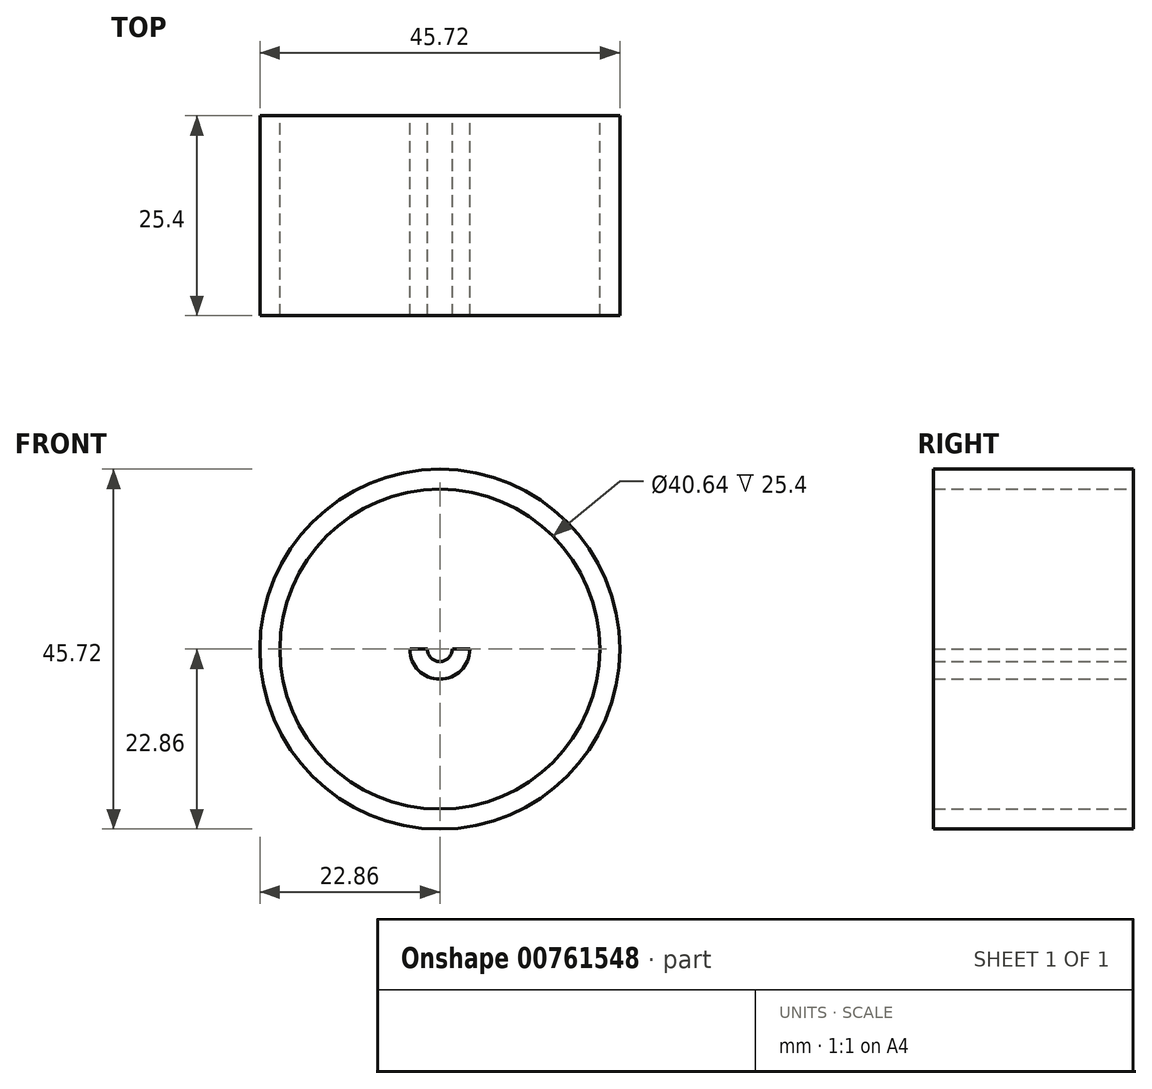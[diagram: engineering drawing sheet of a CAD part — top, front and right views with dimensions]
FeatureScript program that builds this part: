
annotation { "Feature Type Name" : "Feature", "Feature Type Description" : "" }
export const myFeature = defineFeature(function(context is Context, id is Id, definition is map)
    precondition{}
    {
        {
            var Q0;
            Q0=qCreatedBy(makeId("Front.planeOp"),FACE);
            var sketch = newSketch(context, id + "F0", { "sketchPlane" : qUnion([Q0])});
            skCircle(sketch, "E0", {"center": v(0, 0) * mm, "radius": 22.86 * mm});
            skCircle(sketch, "E1", {"center": v(0, 0) * mm, "radius": 1.59 * mm});
            skCircle(sketch, "E2", {"center": v(0, 0) * mm, "radius": 3.81 * mm});
            skCircle(sketch, "E3.0", {"center": v(0, 0) * mm, "radius": 20.32 * mm});
            skLineSegment(sketch, "E4", {"start": v(0, 0) * mm, "end": v(0, 3.81) * mm});
            skLineSegment(sketch, "E5", {"start": v(0, 3.81) * mm, "end": v(0, -3.81) * mm});
            skLineSegment(sketch, "E6", {"start": v(0, -3.81) * mm, "end": v(0, 0) * mm});
            skLineSegment(sketch, "E7", {"start": v(3.81, 0) * mm, "end": v(-3.81, 0) * mm});
            skLineSegment(sketch, "E8", {"start": v(0, 3.8) * mm, "end": v(0, 11.02) * mm});
            skLineSegment(sketch, "E9", {"start": v(-1.49, 15.1) * mm, "end": v(-5.28, 19.62) * mm});
            skPoint(sketch, "E10.newPointA", {"position": v(0, 13.33) * mm});
            skArc(sketch, "E10.filletArc", {"start": v(0, 11.02) * mm, "mid": v(-0.38, 13.2) * mm, "end": v(-1.49, 15.1) * mm});
            skLineSegment(sketch, "E11", {"start": v(0.96, 3.69) * mm, "end": v(3.31, 12.87) * mm});
            skLineSegment(sketch, "E12", {"start": v(2.89, 17.19) * mm, "end": v(1.41, 20.27) * mm});
            skPoint(sketch, "E13.end.orphan", {"position": v(7.48, 13.33) * mm});
            skPoint(sketch, "E14.newPointA", {"position": v(3.89, 15.1) * mm});
            skArc(sketch, "E14.filletArc", {"start": v(3.31, 12.87) * mm, "mid": v(3.48, 15.06) * mm, "end": v(2.89, 17.19) * mm});
            skLineSegment(sketch, "E15", {"start": v(0.55, 7.3) * mm, "end": v(1, 13.07) * mm});
            skLineSegment(sketch, "E16", {"start": v(2.28, 13.03) * mm, "end": v(1.06, 7.23) * mm});
            skLineSegment(sketch, "E17", {"start": v(0.81, 7.03) * mm, "end": v(0.8, 7.03) * mm});
            skLineSegment(sketch, "E18", {"start": v(2.26, 13.24) * mm, "end": v(0.27, 18.44) * mm});
            skLineSegment(sketch, "E19", {"start": v(0.95, 13.3) * mm, "end": v(-1.71, 17.52) * mm});
            skLineSegment(sketch, "E20", {"start": v(-0.71, 18.88) * mm, "end": v(-1.34, 18.64) * mm});
            skPoint(sketch, "E21.start.orphan", {"position": v(-2.74, 19.15) * mm});
            skPoint(sketch, "E22.visualSharp", {"position": v(-2.2, 18.3) * mm});
            skArc(sketch, "E22.filletArc", {"start": v(-1.34, 18.64) * mm, "mid": v(-1.8, 18.17) * mm, "end": v(-1.71, 17.52) * mm});
            skPoint(sketch, "E23.visualSharp", {"position": v(0, 19.15) * mm});
            skArc(sketch, "E23.filletArc", {"start": v(0.27, 18.44) * mm, "mid": v(-0.13, 18.86) * mm, "end": v(-0.71, 18.88) * mm});
            skPoint(sketch, "E24.visualSharp", {"position": v(2.3, 13.14) * mm});
            skArc(sketch, "E24.filletArc", {"start": v(2.28, 13.03) * mm, "mid": v(2.29, 13.13) * mm, "end": v(2.26, 13.24) * mm});
            skPoint(sketch, "E25.visualSharp", {"position": v(1.02, 13.2) * mm});
            skArc(sketch, "E25.filletArc", {"start": v(1, 13.07) * mm, "mid": v(1, 13.2) * mm, "end": v(0.95, 13.3) * mm});
            skPoint(sketch, "E26.visualSharp", {"position": v(0.53, 7.03) * mm});
            skArc(sketch, "E26.filletArc", {"start": v(0.55, 7.3) * mm, "mid": v(0.62, 7.1) * mm, "end": v(0.8, 7.03) * mm});
            skPoint(sketch, "E27.visualSharp", {"position": v(1.02, 7.03) * mm});
            skArc(sketch, "E27.filletArc", {"start": v(0.81, 7.03) * mm, "mid": v(0.97, 7.08) * mm, "end": v(1.06, 7.23) * mm});
            skArc(sketch, "E28.1.0", {"start": v(-11.64, 14.3) * mm, "mid": v(-12.22, 14.37) * mm, "end": v(-12.68, 14) * mm});
            skLineSegment(sketch, "E28.1.1", {"start": v(-12.68, 14) * mm, "end": v(-13, 13.42) * mm});
            skArc(sketch, "E28.1.2", {"start": v(-13, 13.42) * mm, "mid": v(-13.05, 12.77) * mm, "end": v(-12.57, 12.32) * mm});
            skLineSegment(sketch, "E28.1.3", {"start": v(-7.83, 10.8) * mm, "end": v(-12.57, 12.32) * mm});
            skLineSegment(sketch, "E28.1.4", {"start": v(-6.78, 11.6) * mm, "end": v(-11.64, 14.3) * mm});
            skLineSegment(sketch, "E28.1.5", {"start": v(-6.63, 11.44) * mm, "end": v(-3.83, 6.22) * mm});
            skLineSegment(sketch, "E28.1.6", {"start": v(-4.27, 5.95) * mm, "end": v(-7.63, 10.66) * mm});
            skLineSegment(sketch, "E28.1.7", {"start": v(-1.63, 3.44) * mm, "end": v(-5.73, 11.99) * mm});
            skLineSegment(sketch, "E28.1.8", {"start": v(-2.45, 2.92) * mm, "end": v(-7.09, 8.44) * mm});
            skLineSegment(sketch, "E28.1.9", {"start": v(-10.85, 10.62) * mm, "end": v(-16.66, 11.64) * mm});
            skLineSegment(sketch, "E28.1.10", {"start": v(-8.84, 15.02) * mm, "end": v(-11.95, 16.44) * mm});
            skArc(sketch, "E28.1.11", {"start": v(-5.73, 11.99) * mm, "mid": v(-7.02, 13.78) * mm, "end": v(-8.84, 15.02) * mm});
            skArc(sketch, "E28.1.12", {"start": v(-7.09, 8.44) * mm, "mid": v(-8.77, 9.86) * mm, "end": v(-10.85, 10.62) * mm});
            skArc(sketch, "E28.1.13", {"start": v(-6.63, 11.44) * mm, "mid": v(-6.7, 11.53) * mm, "end": v(-6.78, 11.6) * mm});
            skArc(sketch, "E28.1.14", {"start": v(-7.63, 10.66) * mm, "mid": v(-7.72, 10.75) * mm, "end": v(-7.83, 10.8) * mm});
            skArc(sketch, "E28.1.15", {"start": v(-4.27, 5.95) * mm, "mid": v(-4.1, 5.84) * mm, "end": v(-3.9, 5.9) * mm});
            skArc(sketch, "E28.1.16", {"start": v(-3.9, 5.9) * mm, "mid": v(-3.8, 6.05) * mm, "end": v(-3.83, 6.22) * mm});
            skArc(sketch, "E28.2.0", {"start": v(-18.11, 3.47) * mm, "mid": v(-18.6, 3.15) * mm, "end": v(-18.72, 2.58) * mm});
            skLineSegment(sketch, "E28.2.1", {"start": v(-18.72, 2.58) * mm, "end": v(-18.59, 1.92) * mm});
            skArc(sketch, "E28.2.2", {"start": v(-18.59, 1.92) * mm, "mid": v(-18.2, 1.4) * mm, "end": v(-17.55, 1.36) * mm});
            skLineSegment(sketch, "E28.2.3", {"start": v(-12.94, 3.25) * mm, "end": v(-17.55, 1.36) * mm});
            skLineSegment(sketch, "E28.2.4", {"start": v(-12.65, 4.53) * mm, "end": v(-18.11, 3.47) * mm});
            skLineSegment(sketch, "E28.2.5", {"start": v(-12.43, 4.5) * mm, "end": v(-6.93, 2.3) * mm});
            skLineSegment(sketch, "E28.2.6", {"start": v(-7.1, 1.8) * mm, "end": v(-12.7, 3.26) * mm});
            skLineSegment(sketch, "E28.2.7", {"start": v(-3.46, 1.59) * mm, "end": v(-12.1, 5.5) * mm});
            skLineSegment(sketch, "E28.2.8", {"start": v(-3.75, 0.66) * mm, "end": v(-10.86, 1.91) * mm});
            skLineSegment(sketch, "E28.2.9", {"start": v(-15.13, 1.16) * mm, "end": v(-20.24, -1.79) * mm});
            skLineSegment(sketch, "E28.2.10", {"start": v(-16.43, 5.83) * mm, "end": v(-19.72, 4.9) * mm});
            skArc(sketch, "E28.2.11", {"start": v(-12.1, 5.5) * mm, "mid": v(-14.23, 6.05) * mm, "end": v(-16.43, 5.83) * mm});
            skArc(sketch, "E28.2.12", {"start": v(-10.86, 1.91) * mm, "mid": v(-13.06, 1.91) * mm, "end": v(-15.13, 1.16) * mm});
            skArc(sketch, "E28.2.13", {"start": v(-12.43, 4.5) * mm, "mid": v(-12.54, 4.53) * mm, "end": v(-12.65, 4.53) * mm});
            skArc(sketch, "E28.2.14", {"start": v(-12.7, 3.26) * mm, "mid": v(-12.82, 3.27) * mm, "end": v(-12.94, 3.25) * mm});
            skArc(sketch, "E28.2.15", {"start": v(-7.1, 1.8) * mm, "mid": v(-6.9, 1.84) * mm, "end": v(-6.78, 2.01) * mm});
            skArc(sketch, "E28.2.16", {"start": v(-6.78, 2.02) * mm, "mid": v(-6.8, 2.19) * mm, "end": v(-6.93, 2.3) * mm});
            skArc(sketch, "E28.3.0", {"start": v(-16.1, -8.98) * mm, "mid": v(-16.27, -9.54) * mm, "end": v(-16, -10.06) * mm});
            skLineSegment(sketch, "E28.3.1", {"start": v(-16, -10.06) * mm, "end": v(-15.47, -10.48) * mm});
            skArc(sketch, "E28.3.2", {"start": v(-15.47, -10.48) * mm, "mid": v(-14.84, -10.63) * mm, "end": v(-14.32, -10.24) * mm});
            skLineSegment(sketch, "E28.3.3", {"start": v(-12, -5.83) * mm, "end": v(-14.32, -10.24) * mm});
            skLineSegment(sketch, "E28.3.4", {"start": v(-12.6, -4.66) * mm, "end": v(-16.1, -8.98) * mm});
            skLineSegment(sketch, "E28.3.5", {"start": v(-12.42, -4.54) * mm, "end": v(-6.79, -2.7) * mm});
            skLineSegment(sketch, "E28.3.6", {"start": v(-6.6, -3.17) * mm, "end": v(-11.83, -5.66) * mm});
            skLineSegment(sketch, "E28.3.7", {"start": v(-3.67, -1.01) * mm, "end": v(-12.8, -3.56) * mm});
            skLineSegment(sketch, "E28.3.8", {"start": v(-3.3, -1.9) * mm, "end": v(-9.55, -5.51) * mm});
            skLineSegment(sketch, "E28.3.9", {"start": v(-12.34, -8.84) * mm, "end": v(-14.36, -14.38) * mm});
            skLineSegment(sketch, "E28.3.10", {"start": v(-16.33, -6.1) * mm, "end": v(-18.26, -8.91) * mm});
            skArc(sketch, "E28.3.11", {"start": v(-12.8, -3.56) * mm, "mid": v(-14.79, -4.52) * mm, "end": v(-16.33, -6.1) * mm});
            skArc(sketch, "E28.3.12", {"start": v(-9.55, -5.51) * mm, "mid": v(-11.24, -6.93) * mm, "end": v(-12.34, -8.84) * mm});
            skArc(sketch, "E28.3.13", {"start": v(-12.42, -4.54) * mm, "mid": v(-12.52, -4.59) * mm, "end": v(-12.6, -4.66) * mm});
            skArc(sketch, "E28.3.14", {"start": v(-11.83, -5.66) * mm, "mid": v(-11.93, -5.73) * mm, "end": v(-12, -5.83) * mm});
            skArc(sketch, "E28.3.15", {"start": v(-6.6, -3.17) * mm, "mid": v(-6.46, -3.02) * mm, "end": v(-6.49, -2.82) * mm});
            skArc(sketch, "E28.3.16", {"start": v(-6.5, -2.81) * mm, "mid": v(-6.62, -2.7) * mm, "end": v(-6.79, -2.7) * mm});
            skArc(sketch, "E28.4.0", {"start": v(-6.56, -17.23) * mm, "mid": v(-6.33, -17.77) * mm, "end": v(-5.79, -17.98) * mm});
            skLineSegment(sketch, "E28.4.1", {"start": v(-5.79, -17.98) * mm, "end": v(-5.12, -17.97) * mm});
            skArc(sketch, "E28.4.2", {"start": v(-5.12, -17.97) * mm, "mid": v(-4.53, -17.68) * mm, "end": v(-4.38, -17.05) * mm});
            skLineSegment(sketch, "E28.4.3", {"start": v(-5.44, -12.18) * mm, "end": v(-4.38, -17.05) * mm});
            skLineSegment(sketch, "E28.4.4", {"start": v(-6.65, -11.67) * mm, "end": v(-6.56, -17.23) * mm});
            skLineSegment(sketch, "E28.4.5", {"start": v(-6.6, -11.46) * mm, "end": v(-3.47, -6.43) * mm});
            skLineSegment(sketch, "E28.4.6", {"start": v(-3.01, -6.67) * mm, "end": v(-5.42, -11.94) * mm});
            skLineSegment(sketch, "E28.4.7", {"start": v(-2.16, -3.14) * mm, "end": v(-7.52, -10.96) * mm});
            skLineSegment(sketch, "E28.4.8", {"start": v(-1.3, -3.58) * mm, "end": v(-3.77, -10.36) * mm});
            skLineSegment(sketch, "E28.4.9", {"start": v(-3.77, -14.7) * mm, "end": v(-1.75, -20.24) * mm});
            skLineSegment(sketch, "E28.4.10", {"start": v(-8.6, -15.16) * mm, "end": v(-8.26, -18.57) * mm});
            skArc(sketch, "E28.4.11", {"start": v(-7.52, -10.96) * mm, "mid": v(-8.43, -12.96) * mm, "end": v(-8.6, -15.16) * mm});
            skArc(sketch, "E28.4.12", {"start": v(-3.77, -10.36) * mm, "mid": v(-4.15, -12.53) * mm, "end": v(-3.77, -14.7) * mm});
            skArc(sketch, "E28.4.13", {"start": v(-6.6, -11.46) * mm, "mid": v(-6.64, -11.56) * mm, "end": v(-6.65, -11.67) * mm});
            skArc(sketch, "E28.4.14", {"start": v(-5.42, -11.94) * mm, "mid": v(-5.45, -12.06) * mm, "end": v(-5.44, -12.18) * mm});
            skArc(sketch, "E28.4.15", {"start": v(-3.01, -6.67) * mm, "mid": v(-3.01, -6.47) * mm, "end": v(-3.16, -6.33) * mm});
            skArc(sketch, "E28.4.16", {"start": v(-3.17, -6.33) * mm, "mid": v(-3.34, -6.32) * mm, "end": v(-3.47, -6.43) * mm});
            skArc(sketch, "E28.5.0", {"start": v(6.05, -17.42) * mm, "mid": v(6.57, -17.68) * mm, "end": v(7.13, -17.5) * mm});
            skLineSegment(sketch, "E28.5.1", {"start": v(7.13, -17.5) * mm, "end": v(7.63, -17.06) * mm});
            skArc(sketch, "E28.5.2", {"start": v(7.63, -17.06) * mm, "mid": v(7.9, -16.46) * mm, "end": v(7.6, -15.88) * mm});
            skLineSegment(sketch, "E28.5.3", {"start": v(3.66, -12.83) * mm, "end": v(7.6, -15.88) * mm});
            skLineSegment(sketch, "E28.5.4", {"start": v(2.4, -13.22) * mm, "end": v(6.05, -17.42) * mm});
            skLineSegment(sketch, "E28.5.5", {"start": v(2.31, -13.02) * mm, "end": v(1.48, -7.15) * mm});
            skLineSegment(sketch, "E28.5.6", {"start": v(1.98, -7.05) * mm, "end": v(3.52, -12.63) * mm});
            skLineSegment(sketch, "E28.5.7", {"start": v(0.36, -3.8) * mm, "end": v(1.29, -13.22) * mm});
            skLineSegment(sketch, "E28.5.8", {"start": v(1.3, -3.58) * mm, "end": v(3.77, -10.36) * mm});
            skLineSegment(sketch, "E28.5.9", {"start": v(6.56, -13.69) * mm, "end": v(11.67, -16.63) * mm});
            skLineSegment(sketch, "E28.5.10", {"start": v(3.16, -17.14) * mm, "end": v(5.6, -19.53) * mm});
            skArc(sketch, "E28.5.11", {"start": v(1.29, -13.22) * mm, "mid": v(1.88, -15.35) * mm, "end": v(3.16, -17.14) * mm});
            skArc(sketch, "E28.5.12", {"start": v(3.77, -10.36) * mm, "mid": v(4.87, -12.27) * mm, "end": v(6.56, -13.69) * mm});
            skArc(sketch, "E28.5.13", {"start": v(2.31, -13.02) * mm, "mid": v(2.34, -13.12) * mm, "end": v(2.4, -13.22) * mm});
            skArc(sketch, "E28.5.14", {"start": v(3.52, -12.63) * mm, "mid": v(3.58, -12.74) * mm, "end": v(3.66, -12.83) * mm});
            skArc(sketch, "E28.5.15", {"start": v(1.98, -7.05) * mm, "mid": v(1.85, -6.9) * mm, "end": v(1.65, -6.88) * mm});
            skArc(sketch, "E28.5.16", {"start": v(1.64, -6.88) * mm, "mid": v(1.5, -6.99) * mm, "end": v(1.48, -7.15) * mm});
            skArc(sketch, "E28.6.0", {"start": v(15.83, -9.46) * mm, "mid": v(16.4, -9.32) * mm, "end": v(16.7, -8.82) * mm});
            skLineSegment(sketch, "E28.6.1", {"start": v(16.7, -8.82) * mm, "end": v(16.81, -8.16) * mm});
            skArc(sketch, "E28.6.2", {"start": v(16.81, -8.16) * mm, "mid": v(16.63, -7.53) * mm, "end": v(16.03, -7.28) * mm});
            skLineSegment(sketch, "E28.6.3", {"start": v(11.05, -7.48) * mm, "end": v(16.03, -7.28) * mm});
            skLineSegment(sketch, "E28.6.4", {"start": v(10.34, -8.58) * mm, "end": v(15.83, -9.46) * mm});
            skLineSegment(sketch, "E28.6.5", {"start": v(10.14, -8.49) * mm, "end": v(5.73, -4.53) * mm});
            skLineSegment(sketch, "E28.6.6", {"start": v(6.05, -4.13) * mm, "end": v(10.82, -7.4) * mm});
            skLineSegment(sketch, "E28.6.7", {"start": v(2.71, -2.68) * mm, "end": v(9.48, -9.3) * mm});
            skLineSegment(sketch, "E28.6.8", {"start": v(3.3, -1.9) * mm, "end": v(9.55, -5.51) * mm});
            skLineSegment(sketch, "E28.6.9", {"start": v(13.82, -6.27) * mm, "end": v(19.63, -5.24) * mm});
            skLineSegment(sketch, "E28.6.10", {"start": v(13.44, -11.1) * mm, "end": v(16.85, -11.36) * mm});
            skArc(sketch, "E28.6.11", {"start": v(9.48, -9.3) * mm, "mid": v(11.3, -10.55) * mm, "end": v(13.44, -11.1) * mm});
            skArc(sketch, "E28.6.12", {"start": v(9.55, -5.51) * mm, "mid": v(11.62, -6.27) * mm, "end": v(13.82, -6.27) * mm});
            skArc(sketch, "E28.6.13", {"start": v(10.14, -8.49) * mm, "mid": v(10.23, -8.55) * mm, "end": v(10.34, -8.58) * mm});
            skArc(sketch, "E28.6.14", {"start": v(10.82, -7.4) * mm, "mid": v(10.93, -7.46) * mm, "end": v(11.05, -7.48) * mm});
            skArc(sketch, "E28.6.15", {"start": v(6.05, -4.13) * mm, "mid": v(5.85, -4.09) * mm, "end": v(5.68, -4.2) * mm});
            skArc(sketch, "E28.6.16", {"start": v(5.68, -4.22) * mm, "mid": v(5.65, -4.38) * mm, "end": v(5.73, -4.53) * mm});
            skArc(sketch, "E28.7.0", {"start": v(18.2, 2.93) * mm, "mid": v(18.55, 3.4) * mm, "end": v(18.47, 3.98) * mm});
            skLineSegment(sketch, "E28.7.1", {"start": v(18.47, 3.98) * mm, "end": v(18.12, 4.56) * mm});
            skArc(sketch, "E28.7.2", {"start": v(18.12, 4.56) * mm, "mid": v(17.58, 4.92) * mm, "end": v(16.96, 4.73) * mm});
            skLineSegment(sketch, "E28.7.3", {"start": v(13.27, 1.38) * mm, "end": v(16.96, 4.73) * mm});
            skLineSegment(sketch, "E28.7.4", {"start": v(13.43, 0.07) * mm, "end": v(18.2, 2.93) * mm});
            skLineSegment(sketch, "E28.7.5", {"start": v(13.22, 0.02) * mm, "end": v(7.3, 0.21) * mm});
            skLineSegment(sketch, "E28.7.6", {"start": v(7.28, 0.73) * mm, "end": v(13.05, 1.28) * mm});
            skLineSegment(sketch, "E28.7.7", {"start": v(3.8, -0.3) * mm, "end": v(13.25, -1.03) * mm});
            skLineSegment(sketch, "E28.7.8", {"start": v(3.75, 0.66) * mm, "end": v(10.86, 1.91) * mm});
            skLineSegment(sketch, "E28.7.9", {"start": v(14.62, 4.09) * mm, "end": v(18.4, 8.6) * mm});
            skLineSegment(sketch, "E28.7.10", {"start": v(17.43, 0.14) * mm, "end": v(20.2, 2.13) * mm});
            skArc(sketch, "E28.7.11", {"start": v(13.25, -1.03) * mm, "mid": v(15.44, -0.81) * mm, "end": v(17.43, 0.14) * mm});
            skArc(sketch, "E28.7.12", {"start": v(10.86, 1.91) * mm, "mid": v(12.93, 2.67) * mm, "end": v(14.62, 4.09) * mm});
            skArc(sketch, "E28.7.13", {"start": v(13.22, 0.02) * mm, "mid": v(13.33, 0.03) * mm, "end": v(13.43, 0.07) * mm});
            skArc(sketch, "E28.7.14", {"start": v(13.05, 1.28) * mm, "mid": v(13.17, 1.3) * mm, "end": v(13.27, 1.38) * mm});
            skArc(sketch, "E28.7.15", {"start": v(7.28, 0.73) * mm, "mid": v(7.1, 0.63) * mm, "end": v(7.06, 0.43) * mm});
            skArc(sketch, "E28.7.16", {"start": v(7.06, 0.42) * mm, "mid": v(7.14, 0.27) * mm, "end": v(7.3, 0.21) * mm});
            skArc(sketch, "E28.8.0", {"start": v(12.06, 13.95) * mm, "mid": v(12.03, 14.53) * mm, "end": v(11.59, 14.92) * mm});
            skLineSegment(sketch, "E28.8.1", {"start": v(11.59, 14.92) * mm, "end": v(10.95, 15.14) * mm});
            skArc(sketch, "E28.8.2", {"start": v(10.95, 15.14) * mm, "mid": v(10.3, 15.07) * mm, "end": v(9.95, 14.52) * mm});
            skLineSegment(sketch, "E28.8.3", {"start": v(9.28, 9.58) * mm, "end": v(9.95, 14.52) * mm});
            skLineSegment(sketch, "E28.8.4", {"start": v(10.24, 8.69) * mm, "end": v(12.06, 13.95) * mm});
            skLineSegment(sketch, "E28.8.5", {"start": v(10.12, 8.51) * mm, "end": v(5.46, 4.86) * mm});
            skLineSegment(sketch, "E28.8.6", {"start": v(5.11, 5.24) * mm, "end": v(9.18, 9.37) * mm});
            skLineSegment(sketch, "E28.8.7", {"start": v(3.1, 2.2) * mm, "end": v(10.8, 7.73) * mm});
            skLineSegment(sketch, "E28.8.8", {"start": v(2.45, 2.92) * mm, "end": v(7.09, 8.44) * mm});
            skLineSegment(sketch, "E28.8.9", {"start": v(8.57, 12.53) * mm, "end": v(8.57, 18.42) * mm});
            skLineSegment(sketch, "E28.8.10", {"start": v(13.26, 11.3) * mm, "end": v(14.11, 14.62) * mm});
            skArc(sketch, "E28.8.11", {"start": v(10.8, 7.73) * mm, "mid": v(12.35, 9.3) * mm, "end": v(13.26, 11.3) * mm});
            skArc(sketch, "E28.8.12", {"start": v(7.09, 8.44) * mm, "mid": v(8.19, 10.35) * mm, "end": v(8.57, 12.53) * mm});
            skArc(sketch, "E28.8.13", {"start": v(10.12, 8.51) * mm, "mid": v(10.2, 8.6) * mm, "end": v(10.24, 8.69) * mm});
            skArc(sketch, "E28.8.14", {"start": v(9.18, 9.37) * mm, "mid": v(9.25, 9.47) * mm, "end": v(9.28, 9.58) * mm});
            skArc(sketch, "E28.8.15", {"start": v(5.11, 5.24) * mm, "mid": v(5.04, 5.05) * mm, "end": v(5.13, 4.87) * mm});
            skArc(sketch, "E28.8.16", {"start": v(5.14, 4.86) * mm, "mid": v(5.3, 4.8) * mm, "end": v(5.46, 4.86) * mm});
            skSolve(sketch);
        }
        {
            var Q0;
            Q0=makeQuery(id+"F0.imprint","IMPRINT",FACE,{"disambiguationData":[TD([[makeQuery(id+"F0.imprint","IMPRINT",EDGE,{"derivedFrom":sQuery(id+"F0.wireOp",EDGE,"E0")}),1.0]])]});
            var Q1;
            {var subQ3=sQuery(id+"F0.wireOp",EDGE,"E5");var subQ5=sQuery(id+"F0.wireOp",EDGE,"E1");var subQ6=makeQuery(id+"F0.imprint","INTERSECT",VERTEX,{"derivedFrom":[subQ5,subQ3]});Q1=makeQuery(id+"F0.imprint","IMPRINT",FACE,{"disambiguationData":[TD([[makeQuery(id+"F0.imprint","IMPRINT",EDGE,{"disambiguationData":[TD([[subQ6,-1.0]])],"derivedFrom":subQ5}),-1.0]])]});}
            var Q2;
            {var subQ6=sQuery(id+"F0.wireOp",EDGE,"E5");var subQ7=sQuery(id+"F0.wireOp",EDGE,"E1");var subQ8=makeQuery(id+"F0.imprint","INTERSECT",VERTEX,{"derivedFrom":[subQ7,subQ6]});Q2=makeQuery(id+"F0.imprint","IMPRINT",FACE,{"disambiguationData":[TD([[makeQuery(id+"F0.imprint","IMPRINT",EDGE,{"disambiguationData":[TD([[subQ8,1.0]])],"derivedFrom":subQ7}),-1.0]])]});}
            var Q3;
            {var subQ6=sQuery(id+"F0.wireOp",EDGE,"E7");var subQ7=sQuery(id+"F0.wireOp",EDGE,"E1");var subQ8=makeQuery(id+"F0.imprint","INTERSECT",VERTEX,{"disambiguationData":[OD(0.0)],"derivedFrom":[subQ7,subQ6]});Q3=makeQuery(id+"F0.imprint","IMPRINT",FACE,{"disambiguationData":[TD([[makeQuery(id+"F0.imprint","IMPRINT",EDGE,{"disambiguationData":[TD([[subQ8,1.0]])],"derivedFrom":subQ7}),-1.0]])]});}
            var Q4;
            {var subQ4=sQuery(id+"F0.wireOp",EDGE,"E7");var subQ6=sQuery(id+"F0.wireOp",EDGE,"E1");var subQ7=makeQuery(id+"F0.imprint","INTERSECT",VERTEX,{"disambiguationData":[OD(1.0)],"derivedFrom":[subQ6,subQ4]});Q4=makeQuery(id+"F0.imprint","IMPRINT",FACE,{"disambiguationData":[TD([[makeQuery(id+"F0.imprint","IMPRINT",EDGE,{"disambiguationData":[TD([[subQ7,-1.0]])],"derivedFrom":subQ6}),-1.0]])]});}
            extrude(context, id + "F1", {"entities" : qUnion([Q0, Q1, Q2, Q3, Q4]), "depth" : 25.4 * mm, "offsetDistance" : 25.4 * mm});
        }
    });
